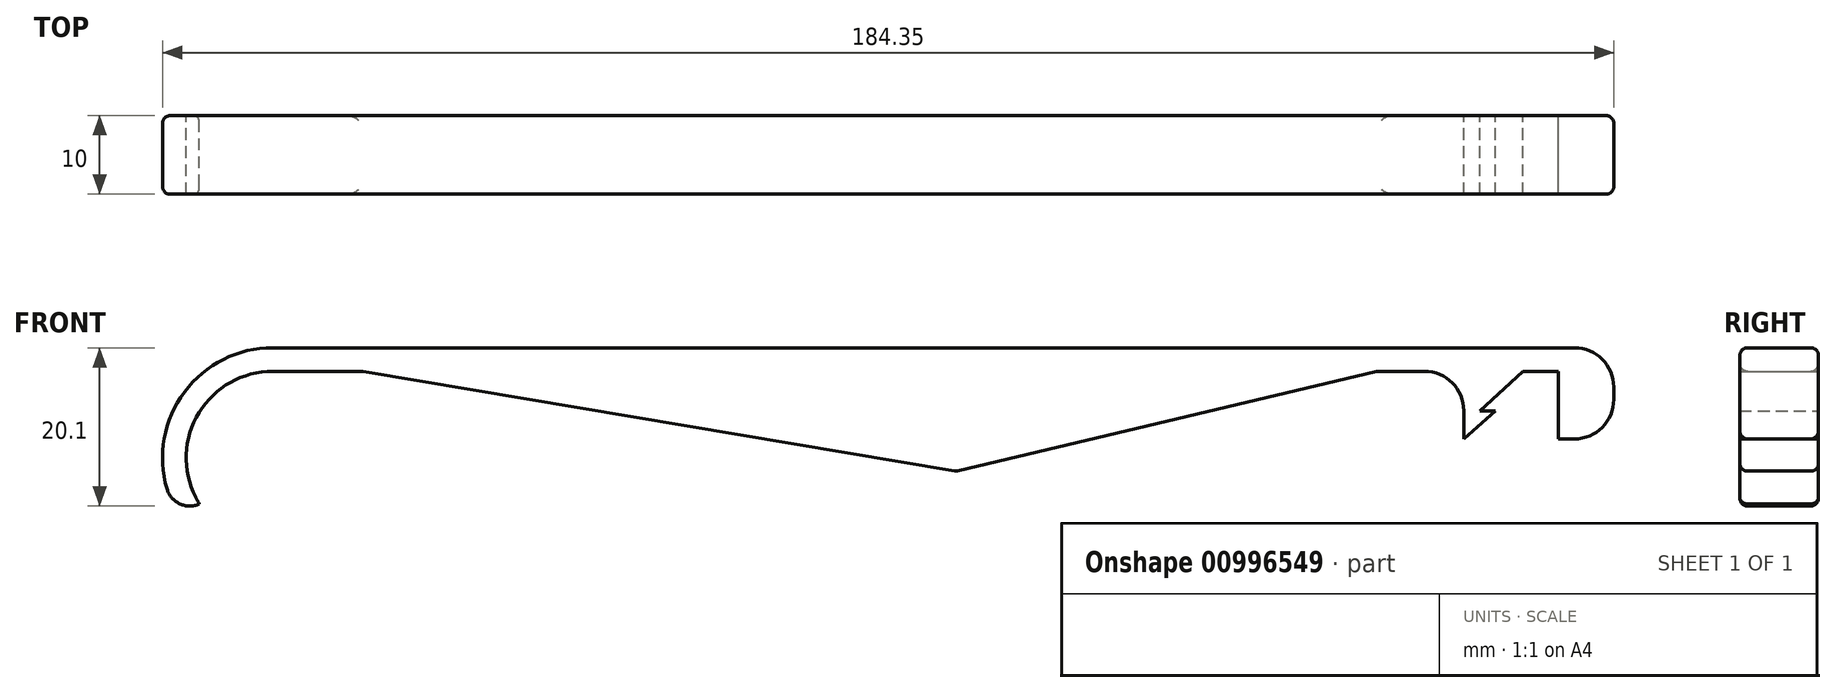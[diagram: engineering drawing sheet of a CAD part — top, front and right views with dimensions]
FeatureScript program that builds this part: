
annotation { "Feature Type Name" : "Feature", "Feature Type Description" : "" }
export const myFeature = defineFeature(function(context is Context, id is Id, definition is map)
    precondition{}
    {
        {
            var Q0;
            Q0=qCreatedBy(makeId("Front.planeOp"),FACE);
            var sketch = newSketch(context, id + "F0", { "sketchPlane" : qUnion([Q0])});
            skArc(sketch, "E0", {"start": v(-86.8, 0) * mm, "mid": v(-96.43, -5.67) * mm, "end": v(-96.13, -16.84) * mm});
            skLineSegment(sketch, "E1", {"start": v(-86.8, 0) * mm, "end": v(64.5, 0) * mm});
            skLineSegment(sketch, "E2", {"start": v(83.54, -3.59) * mm, "end": v(83.54, 3) * mm});
            skLineSegment(sketch, "E3", {"start": v(83.54, 3) * mm, "end": v(-86.8, 3) * mm});
            skArc(sketch, "E4", {"start": v(-86.8, 3) * mm, "mid": v(-99.1, -4.29) * mm, "end": v(-98.59, -18.56) * mm});
            skLineSegment(sketch, "E5", {"start": v(-96.13, -16.84) * mm, "end": v(-98.59, -18.56) * mm});
            skLineSegment(sketch, "E6", {"start": v(66.5, -5) * mm, "end": v(68.5, -5) * mm});
            skLineSegment(sketch, "E7", {"start": v(68.5, -5) * mm, "end": v(64.5, -8.59) * mm});
            skLineSegment(sketch, "E8", {"start": v(64.5, -8.59) * mm, "end": v(64.5, 0) * mm});
            skLineSegment(sketch, "E9", {"start": v(66.5, -5) * mm, "end": v(72, 0) * mm});
            skLineSegment(sketch, "E10.trimOffspring", {"start": v(72, 0) * mm, "end": v(76.5, 0) * mm});
            skLineSegment(sketch, "E11", {"start": v(76.5, 0) * mm, "end": v(76.5, -8.59) * mm});
            skLineSegment(sketch, "E12", {"start": v(76.5, -8.59) * mm, "end": v(78.54, -8.59) * mm});
            skPoint(sketch, "E13.center.orphan", {"position": v(0, 0) * mm});
            skPoint(sketch, "E14.visualSharp", {"position": v(83.54, -8.59) * mm});
            skArc(sketch, "E14.filletArc", {"start": v(78.54, -8.59) * mm, "mid": v(82.08, -7.12) * mm, "end": v(83.54, -3.59) * mm});
            skSolve(sketch);
        }
        {
            var Q0;
            Q0 = qSketchRegion(id + "F0", true);
            extrude(context, id + "F1", {"entities" : qUnion([Q0]), "depth" : 5 * mm, "offsetDistance" : 25 * mm, "hasSecondDirection" : true, "secondDirectionOppositeDirection" : true, "secondDirectionDepth" : 5 * mm});
        }
        {
            var Q0;
            Q0=qCreatedBy(makeId("Front.planeOp"),FACE);
            var sketch = newSketch(context, id + "F2", { "sketchPlane" : qUnion([Q0])});
            skLineSegment(sketch, "E15", {"start": v(0, -12.7) * mm, "end": v(53.51, 0) * mm});
            skLineSegment(sketch, "E16", {"start": v(0, -12.7) * mm, "end": v(-75.42, 0) * mm});
            skLineSegment(sketch, "E17", {"start": v(-75.42, 0) * mm, "end": v(53.51, 0) * mm});
            skSolve(sketch);
        }
        {
            var Q0;
            Q0 = qSketchRegion(id + "F2", true);
            extrude(context, id + "F3", {"entities" : qUnion([Q0]), "operationType" : NewBodyOperationType.ADD, "depth" : 5 * mm, "offsetDistance" : 25 * mm, "hasSecondDirection" : true, "secondDirectionOppositeDirection" : true, "secondDirectionDepth" : 5 * mm});
        }
        {
            var Q0;
            Q0=makeQuery(id+"F1.opExtrude","SWEPT_EDGE",EDGE,{"disambiguationData":[OSD([sQuery(id+"F0.wireOp",EDGE,"E4"),sQuery(id+"F0.wireOp",EDGE,"E5")])]});
            fillet(context, id + "F4", {"entities" : qUnion([Q0]), "radius" : 3 * mm, "tangentPropagation" : true, "allowEdgeOverflow" : false});
        }
        {
            var Q0;
            Q0=makeQuery(id+"F1.opExtrude","SWEPT_EDGE",EDGE,{"disambiguationData":[OSD([sQuery(id+"F0.wireOp",EDGE,"E2"),sQuery(id+"F0.wireOp",EDGE,"E3")])]});
            fillet(context, id + "F5", {"entities" : qUnion([Q0]), "radius" : 5 * mm, "tangentPropagation" : true, "allowEdgeOverflow" : false});
        }
        {
            var Q0;
            Q0=makeQuery(id+"F1.opExtrude","SWEPT_FACE",FACE,{"disambiguationData":[OSD([sQuery(id+"F0.wireOp",EDGE,"E3")])]});
            fillet(context, id + "F6", {"entities" : qUnion([Q0]), "radius" : 1 * mm, "tangentPropagation" : true, "allowEdgeOverflow" : false});
        }
        {
            var Q0;
            Q0=makeQuery(id+"F3.opExtrude","SWEPT_FACE",FACE,{"disambiguationData":[OSD([sQuery(id+"F2.wireOp",EDGE,"E16")])]});
            var Q1;
            Q1=makeQuery(id+"F3.opExtrude","SWEPT_FACE",FACE,{"disambiguationData":[OSD([sQuery(id+"F2.wireOp",EDGE,"E15")])]});
            fillet(context, id + "F7", {"entities" : qUnion([Q0, Q1]), "radius" : 1 * mm, "tangentPropagation" : true, "allowEdgeOverflow" : false});
        }
        {
            var Q0;
            Q0=makeQuery(id+"F1.opExtrude","SWEPT_EDGE",EDGE,{"disambiguationData":[OSD([sQuery(id+"F0.wireOp",EDGE,"E1"),sQuery(id+"F0.wireOp",EDGE,"E8")])]});
            fillet(context, id + "F8", {"entities" : qUnion([Q0]), "radius" : 5 * mm, "tangentPropagation" : true, "allowEdgeOverflow" : false});
        }
    });
